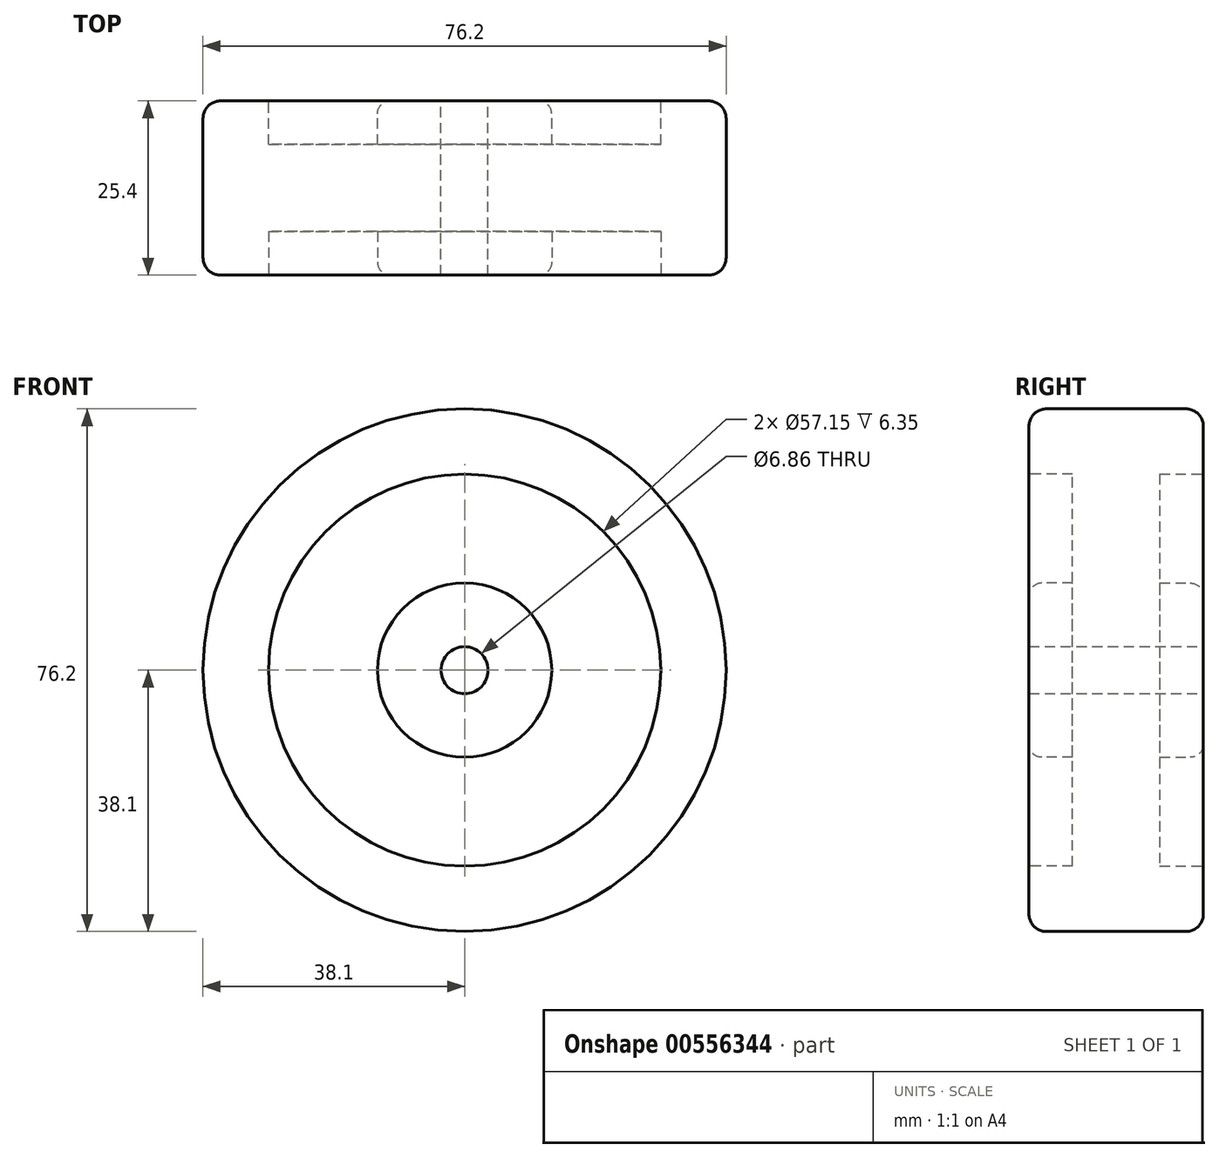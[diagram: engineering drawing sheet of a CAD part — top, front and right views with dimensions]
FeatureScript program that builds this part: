
annotation { "Feature Type Name" : "Feature", "Feature Type Description" : "" }
export const myFeature = defineFeature(function(context is Context, id is Id, definition is map)
    precondition{}
    {
        {
            var Q0;
            Q0=qCreatedBy(makeId("Front.planeOp"),FACE);
            var sketch = newSketch(context, id + "F0", { "sketchPlane" : qUnion([Q0])});
            skCircle(sketch, "E0", {"center": v(0, 0) * mm, "radius": 38.1 * mm});
            skCircle(sketch, "E1", {"center": v(0, 0) * mm, "radius": 3.43 * mm});
            skSolve(sketch);
        }
        {
            var Q0;
            Q0=makeQuery(id+"F0.imprint","IMPRINT",FACE,{"disambiguationData":[TD([[makeQuery(id+"F0.imprint","IMPRINT",EDGE,{"derivedFrom":sQuery(id+"F0.wireOp",EDGE,"E0")}),1.0]])]});
            extrude(context, id + "F1", {"entities" : qUnion([Q0]), "depth" : 25.4 * mm, "offsetDistance" : 25.4 * mm});
        }
        {
            var Q0;
            Q0=makeQuery(id+"F1.opExtrude","CAP_FACE",FACE,{"disambiguationData":[OSD([sQuery(id+"F0.wireOp",EDGE,"E0"),sQuery(id+"F0.wireOp",EDGE,"E1")])],"isStart":false});
            var sketch = newSketch(context, id + "F2", { "sketchPlane" : qUnion([Q0])});
            skCircle(sketch, "E2", {"center": v(0, 0) * mm, "radius": 28.58 * mm});
            skCircle(sketch, "E3", {"center": v(0, 0) * mm, "radius": 12.7 * mm});
            skSolve(sketch);
        }
        {
            var Q0;
            Q0=makeQuery(id+"F2.imprint","IMPRINT",FACE,{"disambiguationData":[TD([[makeQuery(id+"F2.imprint","IMPRINT",EDGE,{"derivedFrom":sQuery(id+"F2.wireOp",EDGE,"E2")}),1.0]])]});
            extrude(context, id + "F3", {"entities" : qUnion([Q0]), "operationType" : NewBodyOperationType.REMOVE, "oppositeDirection" : true, "depth" : 6.35 * mm, "offsetDistance" : 25.4 * mm});
        }
        {
            var Q0;
            Q0=makeQuery(id+"F1.opExtrude","CAP_FACE",FACE,{"disambiguationData":[OSD([sQuery(id+"F0.wireOp",EDGE,"E0"),sQuery(id+"F0.wireOp",EDGE,"E1")])],"isStart":true});
            var sketch = newSketch(context, id + "F4", { "sketchPlane" : qUnion([Q0])});
            skCircle(sketch, "E4", {"center": v(0, 0) * mm, "radius": 28.58 * mm});
            skCircle(sketch, "E5", {"center": v(0, 0) * mm, "radius": 12.7 * mm});
            skSolve(sketch);
        }
        {
            var Q0;
            Q0=makeQuery(id+"F4.imprint","IMPRINT",FACE,{"disambiguationData":[TD([[makeQuery(id+"F4.imprint","IMPRINT",EDGE,{"derivedFrom":sQuery(id+"F4.wireOp",EDGE,"E4")}),1.0]])]});
            extrude(context, id + "F5", {"entities" : qUnion([Q0]), "operationType" : NewBodyOperationType.REMOVE, "oppositeDirection" : true, "depth" : 6.35 * mm, "offsetDistance" : 25.4 * mm});
        }
        {
            var Q0;
            Q0=makeQuery(id+"F5.boolean.opBoolean","COPY",EDGE,{"derivedFrom":makeQuery(id+"F5.opExtrude","CAP_EDGE",EDGE,{"disambiguationData":[OSD([sQuery(id+"F4.wireOp",EDGE,"E4")])],"isStart":true})});
            var Q1;
            Q1=makeQuery(id+"F5.boolean.opBoolean","COPY",EDGE,{"derivedFrom":makeQuery(id+"F5.opExtrude","CAP_EDGE",EDGE,{"disambiguationData":[OSD([sQuery(id+"F0.wireOp",EDGE,"E1")])],"isStart":false})});
            var Q2;
            Q2=makeQuery(id+"F1.opExtrude","CAP_EDGE",EDGE,{"disambiguationData":[OSD([sQuery(id+"F0.wireOp",EDGE,"E0")])],"isStart":true});
            var Q3;
            Q3=makeQuery(id+"F1.opExtrude","CAP_EDGE",EDGE,{"disambiguationData":[OSD([sQuery(id+"F0.wireOp",EDGE,"E0")])],"isStart":false});
            var Q4;
            Q4=makeQuery(id+"F3.boolean.opBoolean","COPY",EDGE,{"derivedFrom":makeQuery(id+"F3.opExtrude","CAP_EDGE",EDGE,{"disambiguationData":[OSD([sQuery(id+"F2.wireOp",EDGE,"E2")])],"isStart":true})});
            var Q5;
            Q5=makeQuery(id+"F3.boolean.opBoolean","COPY",EDGE,{"derivedFrom":makeQuery(id+"F3.opExtrude","CAP_EDGE",EDGE,{"disambiguationData":[OSD([sQuery(id+"F0.wireOp",EDGE,"E1")])],"isStart":false})});
            fillet(context, id + "F6", {"entities" : qUnion([Q0, Q1, Q2, Q3, Q4, Q5]), "radius" : 2.54 * mm, "tangentPropagation" : true, "allowEdgeOverflow" : false});
        }
        {
            var Q0;
            Q0=makeQuery(id+"F3.boolean.opBoolean","COPY",EDGE,{"derivedFrom":makeQuery(id+"F3.opExtrude","CAP_EDGE",EDGE,{"disambiguationData":[OSD([sQuery(id+"F2.wireOp",EDGE,"E3")])],"isStart":true})});
            var Q1;
            Q1=makeQuery(id+"F5.boolean.opBoolean","COPY",EDGE,{"derivedFrom":makeQuery(id+"F5.opExtrude","CAP_EDGE",EDGE,{"disambiguationData":[OSD([sQuery(id+"F4.wireOp",EDGE,"E5")])],"isStart":true})});
            fillet(context, id + "F7", {"entities" : qUnion([Q0, Q1]), "radius" : 1.9 * mm, "tangentPropagation" : true, "allowEdgeOverflow" : false});
        }
    });
